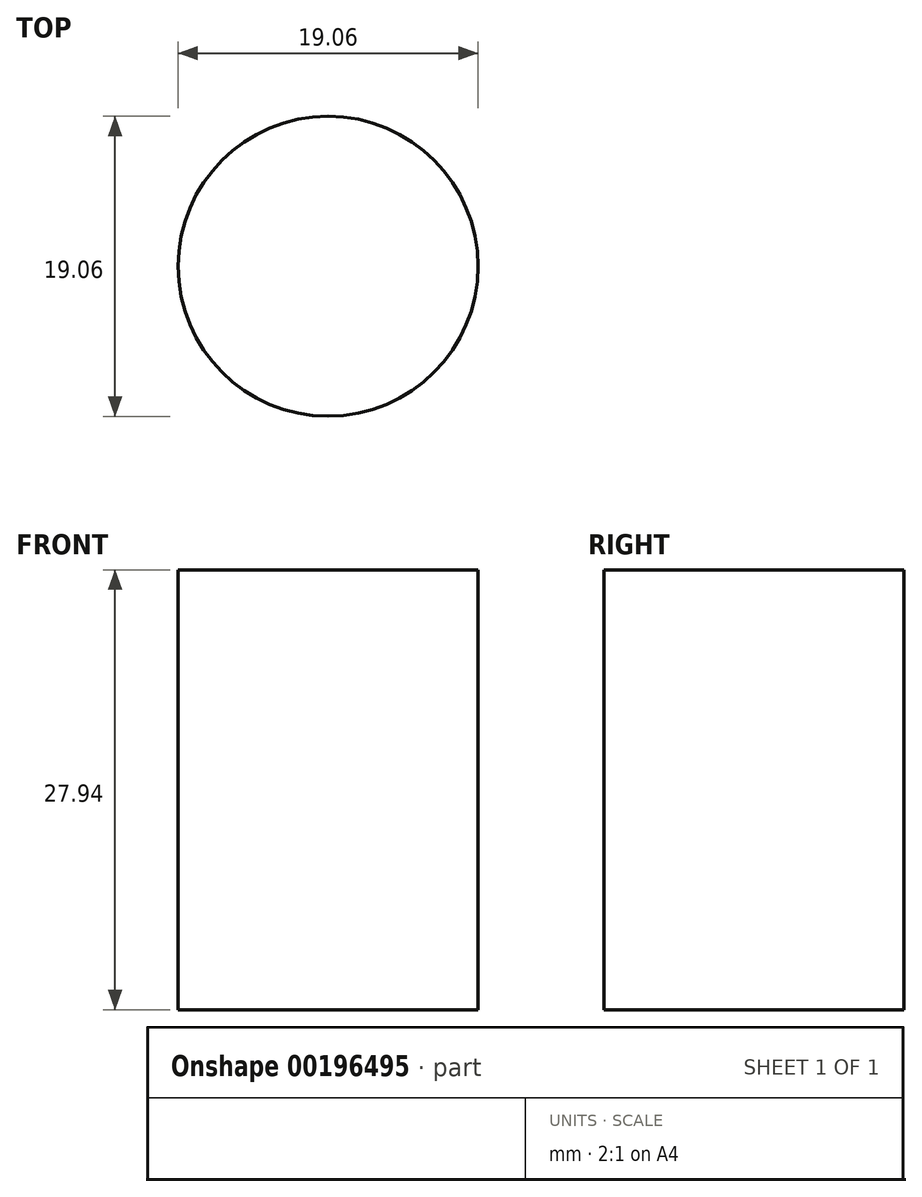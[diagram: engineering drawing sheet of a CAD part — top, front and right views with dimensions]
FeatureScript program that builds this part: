
annotation { "Feature Type Name" : "Feature", "Feature Type Description" : "" }
export const myFeature = defineFeature(function(context is Context, id is Id, definition is map)
    precondition{}
    {
        {
            var Q0;
            Q0=qCreatedBy(makeId("Top.planeOp"),FACE);
            var sketch = newSketch(context, id + "F0", { "sketchPlane" : qUnion([Q0])});
            skCircle(sketch, "E0", {"center": v(0, 0) * mm, "radius": 9.53 * mm});
            skSolve(sketch);
        }
        {
            var Q0;
            Q0=makeQuery(id+"F0.imprint","IMPRINT",FACE,{"disambiguationData":[TD([[makeQuery(id+"F0.imprint","IMPRINT",EDGE,{"derivedFrom":sQuery(id+"F0.wireOp",EDGE,"E0")}),1.0]])]});
            extrude(context, id + "F1", {"entities" : qUnion([Q0]), "endBound" : BoundingType.SYMMETRIC, "depth" : 27.94 * mm});
        }
    });
